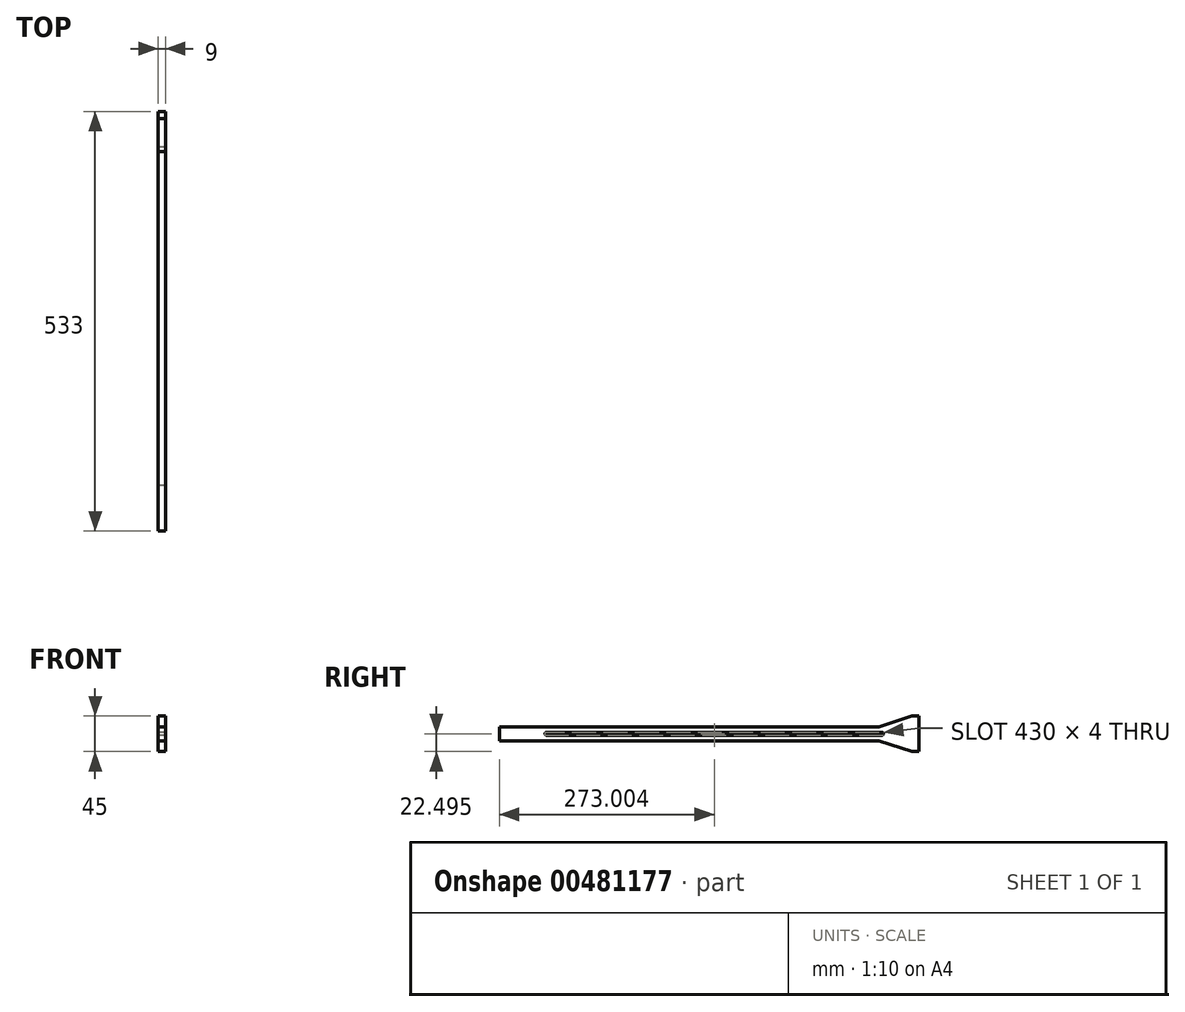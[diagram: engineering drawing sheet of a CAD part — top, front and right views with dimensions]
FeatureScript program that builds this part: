
annotation { "Feature Type Name" : "Feature", "Feature Type Description" : "" }
export const myFeature = defineFeature(function(context is Context, id is Id, definition is map)
    precondition{}
    {
        {
            var Q0;
            Q0=qCreatedBy(makeId("Right.planeOp"),FACE);
            var sketch = newSketch(context, id + "F0", { "sketchPlane" : qUnion([Q0])});
            skLineSegment(sketch, "E0.bottom", {"start": v(111.57, 42.6) * mm, "end": v(102.57, 42.6) * mm});
            skLineSegment(sketch, "E0.top", {"start": v(111.57, -2.4) * mm, "end": v(102.57, -2.4) * mm});
            skLineSegment(sketch, "E0.left", {"start": v(111.57, 42.6) * mm, "end": v(111.57, -2.4) * mm});
            skLineSegment(sketch, "E1", {"start": v(64.57, 22.1) * mm, "end": v(-361.43, 22.1) * mm});
            skLineSegment(sketch, "E2", {"start": v(-361.43, 18.1) * mm, "end": v(64.57, 18.1) * mm});
            skLineSegment(sketch, "E3", {"start": v(102.57, 42.6) * mm, "end": v(60.57, 29.1) * mm});
            skLineSegment(sketch, "E4", {"start": v(102.57, -2.4) * mm, "end": v(60.57, 11.1) * mm});
            skArc(sketch, "E5", {"start": v(64.57, 22.1) * mm, "mid": v(66.57, 20.1) * mm, "end": v(64.57, 18.1) * mm});
            skArc(sketch, "E6", {"start": v(-361.43, 22.1) * mm, "mid": v(-363.43, 20.1) * mm, "end": v(-361.43, 18.1) * mm});
            skLineSegment(sketch, "E7", {"start": v(60.57, 29.1) * mm, "end": v(-405.43, 29.1) * mm});
            skLineSegment(sketch, "E8", {"start": v(60.57, 11.1) * mm, "end": v(-405.43, 11.1) * mm});
            skLineSegment(sketch, "E9", {"start": v(-361.43, 29.1) * mm, "end": v(-421.43, 29.1) * mm});
            skLineSegment(sketch, "E10", {"start": v(-361.43, 11.1) * mm, "end": v(-421.43, 11.1) * mm});
            skLineSegment(sketch, "E11", {"start": v(-421.43, 29.1) * mm, "end": v(-421.43, 11.1) * mm});
            skSolve(sketch);
        }
        {
            var Q0;
            Q0=makeQuery(id+"F0.imprint","IMPRINT",FACE,{"disambiguationData":[TD([[makeQuery(id+"F0.imprint","IMPRINT",EDGE,{"derivedFrom":sQuery(id+"F0.wireOp",EDGE,"E0.bottom")}),1.0]])]});
            extrude(context, id + "F1", {"entities" : qUnion([Q0]), "depth" : 9 * mm, "offsetDistance" : 25 * mm});
        }
    });
